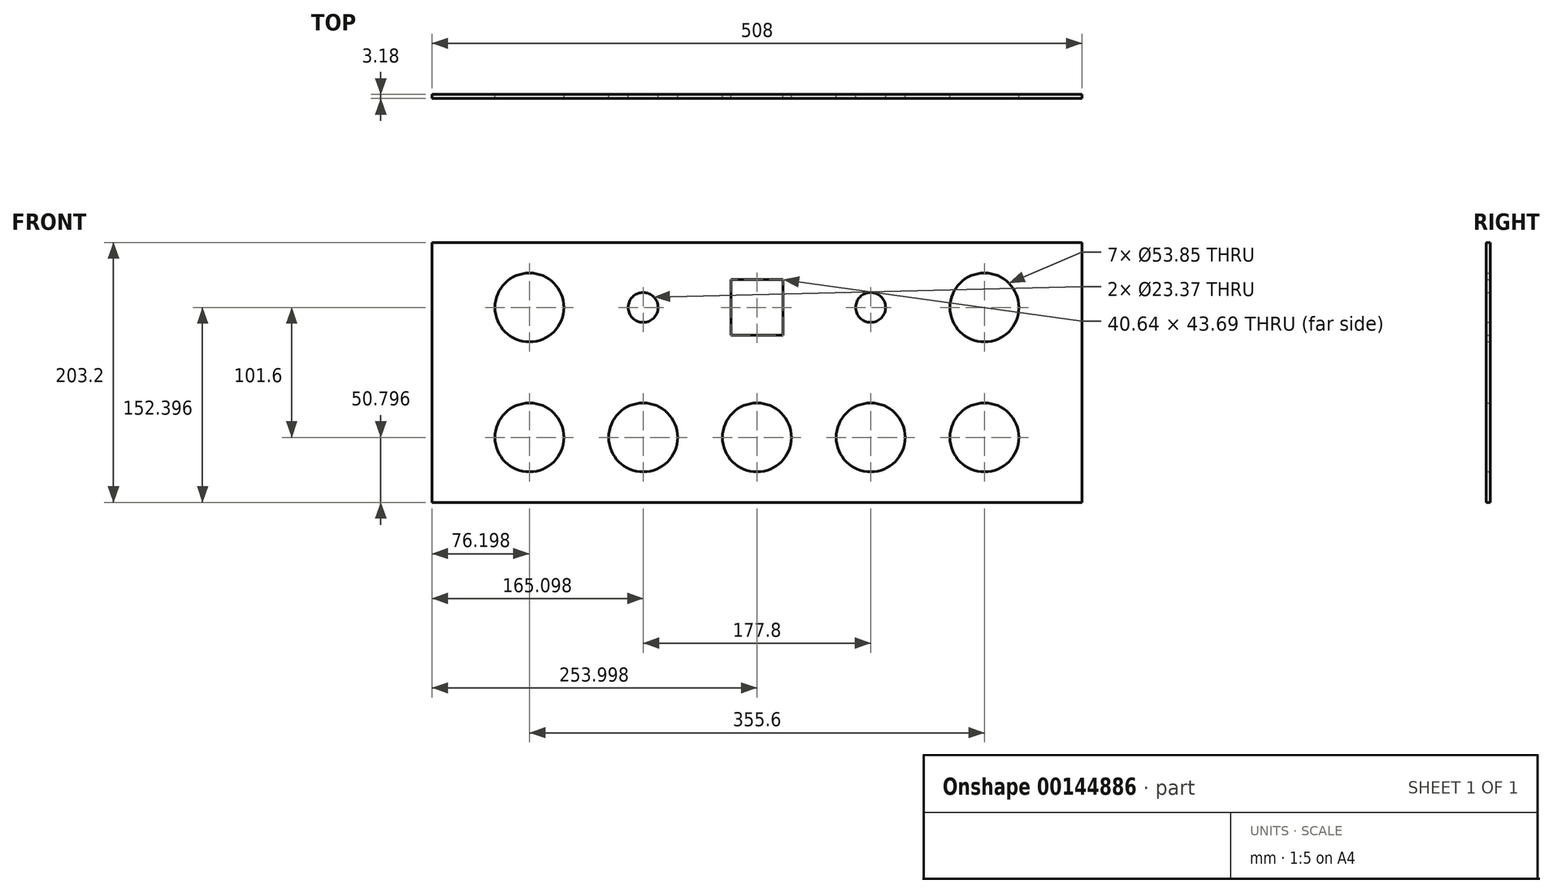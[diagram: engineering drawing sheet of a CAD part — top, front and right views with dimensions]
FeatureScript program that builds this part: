
annotation { "Feature Type Name" : "Feature", "Feature Type Description" : "" }
export const myFeature = defineFeature(function(context is Context, id is Id, definition is map)
    precondition{}
    {
        {
            var Q0;
            Q0=qCreatedBy(makeId("Front.planeOp"),FACE);
            var sketch = newSketch(context, id + "F0", { "sketchPlane" : qUnion([Q0])});
            skLineSegment(sketch, "E0.bottom", {"start": v(-382.28, 164.78) * mm, "end": v(125.72, 164.78) * mm});
            skLineSegment(sketch, "E0.top", {"start": v(-382.28, -38.42) * mm, "end": v(125.72, -38.42) * mm});
            skLineSegment(sketch, "E0.left", {"start": v(-382.28, 164.78) * mm, "end": v(-382.28, -38.42) * mm});
            skLineSegment(sketch, "E0.right", {"start": v(125.72, 164.78) * mm, "end": v(125.72, -38.42) * mm});
            skLineSegment(sketch, "E1.0", {"start": v(-382.28, 113.98) * mm, "end": v(125.72, 113.98) * mm, "construction": true});
            skLineSegment(sketch, "E2.0", {"start": v(-382.28, 12.38) * mm, "end": v(125.72, 12.38) * mm, "construction": true});
            skLineSegment(sketch, "E3.0", {"start": v(-306.08, 164.78) * mm, "end": v(-306.08, -38.42) * mm, "construction": true});
            skLineSegment(sketch, "E4.0", {"start": v(49.52, 164.78) * mm, "end": v(49.52, -38.42) * mm, "construction": true});
            skLineSegment(sketch, "E5", {"start": v(-128.28, 164.78) * mm, "end": v(-128.28, -38.42) * mm, "construction": true});
            skLineSegment(sketch, "E6.0", {"start": v(-217.18, 164.78) * mm, "end": v(-217.18, -38.42) * mm, "construction": true});
            skLineSegment(sketch, "E7.0", {"start": v(-39.38, 164.78) * mm, "end": v(-39.38, -38.42) * mm, "construction": true});
            skCircle(sketch, "E8", {"center": v(-306.08, 113.98) * mm, "radius": 26.92 * mm});
            skCircle(sketch, "E9", {"center": v(-217.18, 113.98) * mm, "radius": 11.68 * mm});
            skCircle(sketch, "E10", {"center": v(-39.38, 113.98) * mm, "radius": 11.68 * mm});
            skCircle(sketch, "E11", {"center": v(49.52, 113.98) * mm, "radius": 26.92 * mm});
            skCircle(sketch, "E12", {"center": v(-306.08, 12.38) * mm, "radius": 26.92 * mm});
            skCircle(sketch, "E13", {"center": v(-217.18, 12.38) * mm, "radius": 26.92 * mm});
            skCircle(sketch, "E14", {"center": v(-128.28, 12.38) * mm, "radius": 26.92 * mm});
            skCircle(sketch, "E15", {"center": v(-39.38, 12.38) * mm, "radius": 26.92 * mm});
            skCircle(sketch, "E16", {"center": v(49.52, 12.38) * mm, "radius": 26.92 * mm});
            skLineSegment(sketch, "E17.0", {"start": v(-382.28, 92.13) * mm, "end": v(125.72, 92.13) * mm, "construction": true});
            skLineSegment(sketch, "E18.0", {"start": v(-382.28, 135.82) * mm, "end": v(125.72, 135.82) * mm, "construction": true});
            skLineSegment(sketch, "E19.0", {"start": v(-148.6, 164.78) * mm, "end": v(-148.6, -38.42) * mm, "construction": true});
            skLineSegment(sketch, "E20.0", {"start": v(-107.96, 164.78) * mm, "end": v(-107.96, -38.42) * mm, "construction": true});
            skLineSegment(sketch, "E21.bottom", {"start": v(-148.6, 135.82) * mm, "end": v(-107.96, 135.82) * mm});
            skLineSegment(sketch, "E21.top", {"start": v(-148.6, 92.13) * mm, "end": v(-107.96, 92.13) * mm});
            skLineSegment(sketch, "E21.left", {"start": v(-148.6, 135.82) * mm, "end": v(-148.6, 92.13) * mm});
            skLineSegment(sketch, "E21.right", {"start": v(-107.96, 135.82) * mm, "end": v(-107.96, 92.13) * mm});
            skSolve(sketch);
        }
        {
            var Q0;
            Q0=makeQuery(id+"F0.imprint","IMPRINT",FACE,{"disambiguationData":[TD([[makeQuery(id+"F0.imprint","IMPRINT",EDGE,{"derivedFrom":sQuery(id+"F0.wireOp",EDGE,"E0.bottom")}),-1.0]])]});
            extrude(context, id + "F1", {"entities" : qUnion([Q0]), "depth" : 3.17 * mm});
        }
    });
